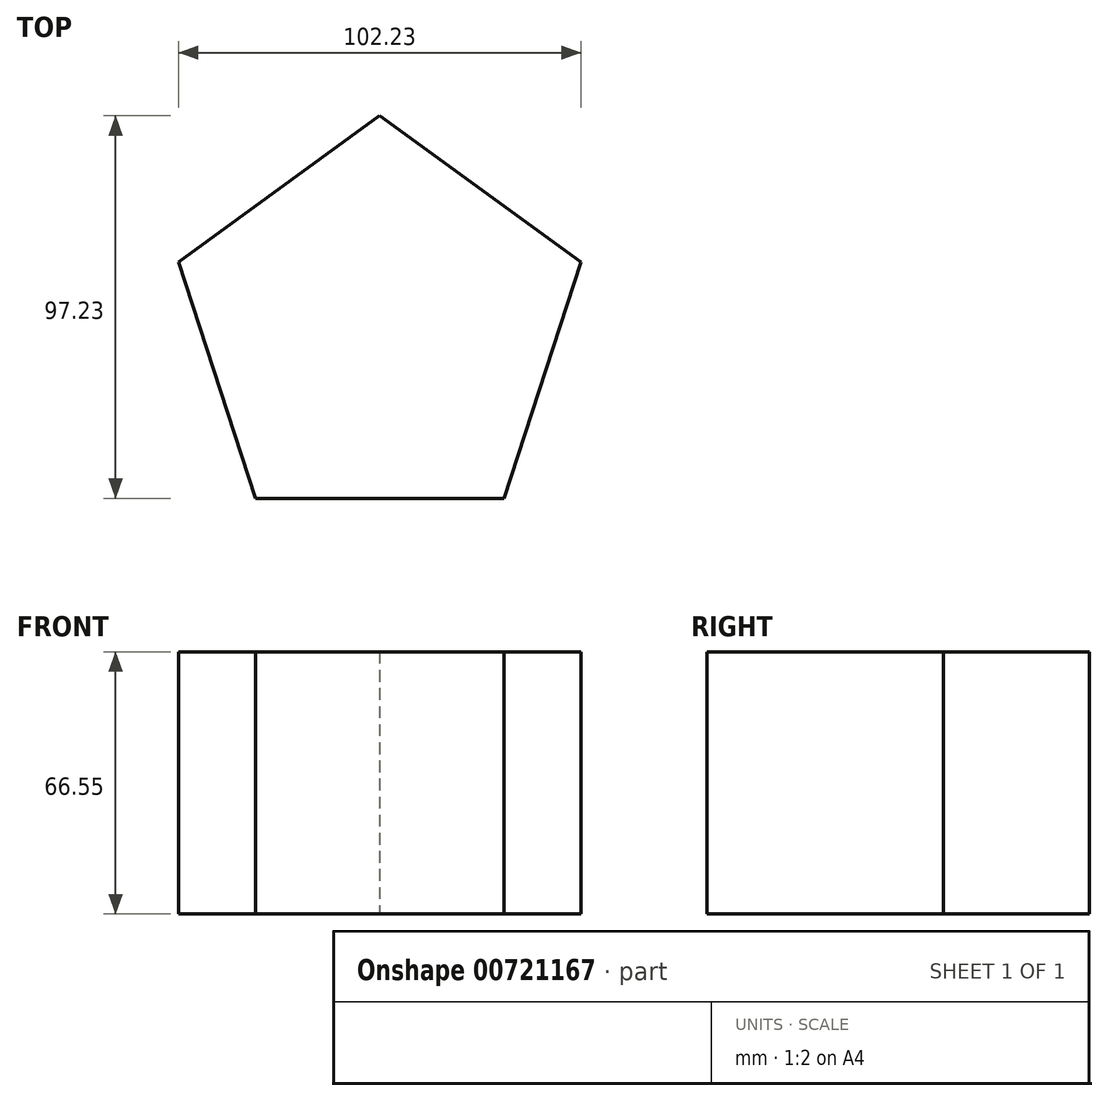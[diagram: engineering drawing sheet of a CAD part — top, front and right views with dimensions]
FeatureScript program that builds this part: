
annotation { "Feature Type Name" : "Feature", "Feature Type Description" : "" }
export const myFeature = defineFeature(function(context is Context, id is Id, definition is map)
    precondition{}
    {
        {
            var Q0;
            Q0=qCreatedBy(makeId("Top.planeOp"),FACE);
            var sketch = newSketch(context, id + "F0", { "sketchPlane" : qUnion([Q0])});
            skCircle(sketch, "E0.cCircle", {"center": v(-26.63, 0) * mm, "radius": 43.48 * mm, "construction": true});
            skLineSegment(sketch, "E0.0", {"start": v(4.97, -43.48) * mm, "end": v(-58.22, -43.48) * mm});
            skLineSegment(sketch, "E0.1", {"start": v(-58.22, -43.48) * mm, "end": v(-77.74, 16.6) * mm});
            skLineSegment(sketch, "E0.2", {"start": v(-77.74, 16.6) * mm, "end": v(-26.63, 53.75) * mm});
            skLineSegment(sketch, "E0.3", {"start": v(-26.63, 53.75) * mm, "end": v(24.49, 16.6) * mm});
            skLineSegment(sketch, "E0.4", {"start": v(24.49, 16.6) * mm, "end": v(4.97, -43.48) * mm});
            skPoint(sketch, "E0.0.midPoint", {"position": v(-26.63, -43.48) * mm});
            skSolve(sketch);
        }
        {
            var Q0;
            Q0 = qSketchRegion(id + "F0", true);
            extrude(context, id + "F1", {"entities" : qUnion([Q0]), "depth" : 66.55 * mm, "offsetDistance" : 25.4 * mm});
        }
    });
